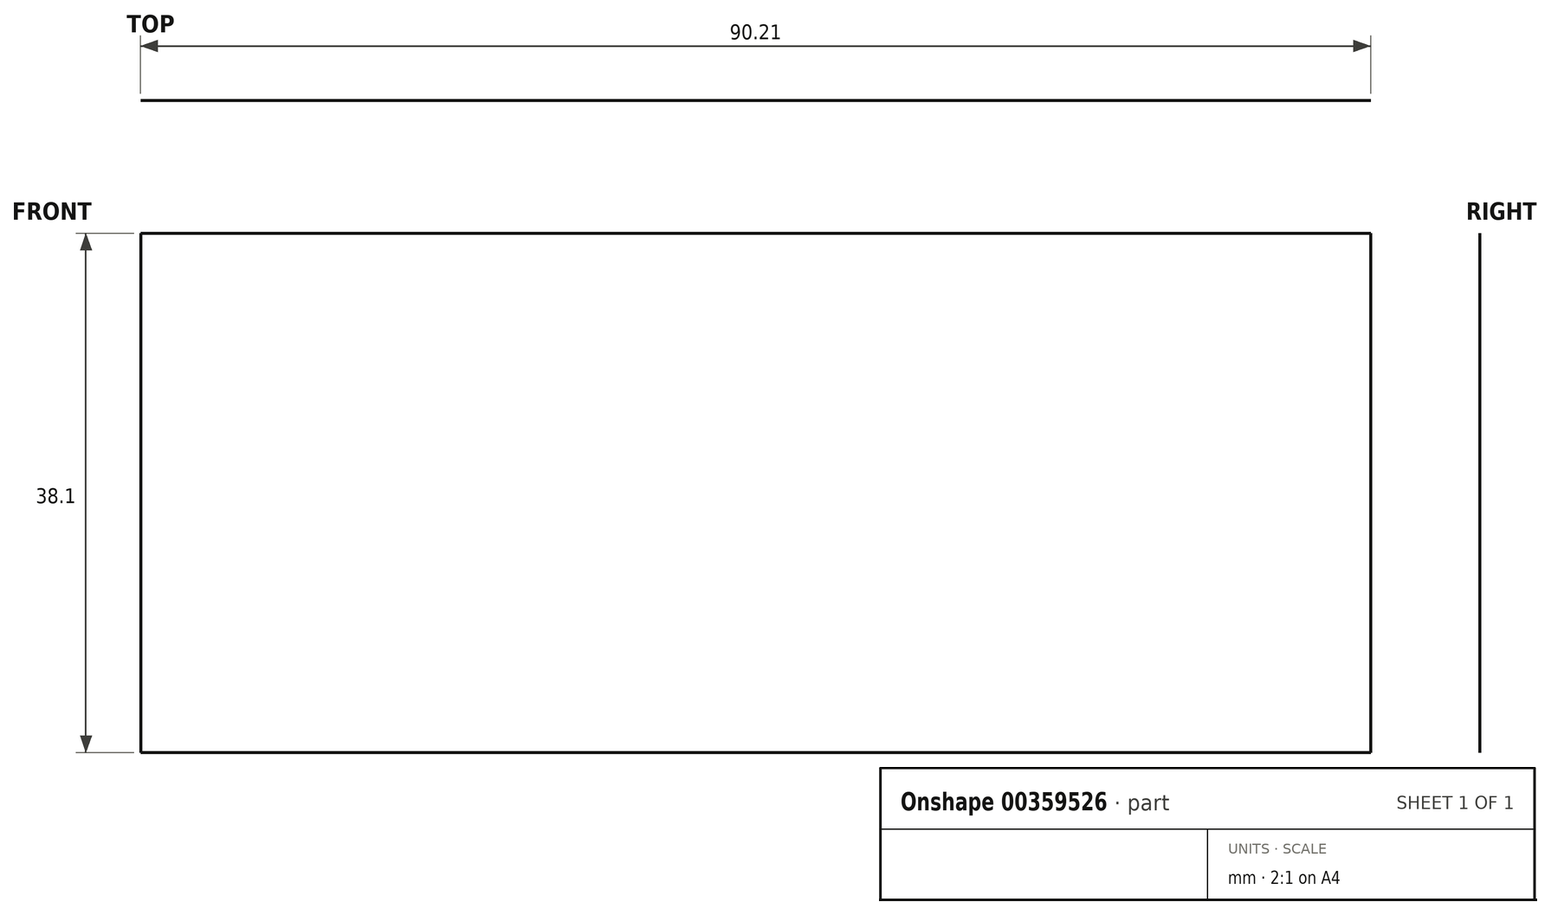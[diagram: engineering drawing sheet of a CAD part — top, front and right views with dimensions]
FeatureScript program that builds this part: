
annotation { "Feature Type Name" : "Feature", "Feature Type Description" : "" }
export const myFeature = defineFeature(function(context is Context, id is Id, definition is map)
    precondition{}
    {
        {
            var Q0;
            Q0=qCreatedBy(makeId("Top.planeOp"),FACE);
            var sketch = newSketch(context, id + "F0", { "sketchPlane" : qUnion([Q0])});
            skLineSegment(sketch, "E0.bottom", {"start": v(35.87, 55.2) * mm, "end": v(-54.34, 55.2) * mm});
            skLineSegment(sketch, "E0.top", {"start": v(35.87, 0) * mm, "end": v(-54.34, 0) * mm});
            skLineSegment(sketch, "E0.left", {"start": v(35.87, 55.2) * mm, "end": v(35.87, 0) * mm});
            skLineSegment(sketch, "E0.right", {"start": v(-54.34, 55.2) * mm, "end": v(-54.34, 0) * mm});
            skSolve(sketch);
        }
        {
            var Q0;
            Q0=makeQuery(id+"F0.imprint","IMPRINT",FACE,{"disambiguationData":[TD([[makeQuery(id+"F0.imprint","IMPRINT",EDGE,{"derivedFrom":sQuery(id+"F0.wireOp",EDGE,"E0.bottom")}),1.0]])]});
            var Q1;
            Q1=sQuery(id+"F0.wireOp",EDGE,"E0.bottom");
            extrude(context, id + "F1", {"entities" : qUnion([Q0]), "bodyType" : ToolBodyType.SURFACE, "surfaceEntities" : qUnion([Q1]), "depth" : 38.1 * mm});
        }
    });
